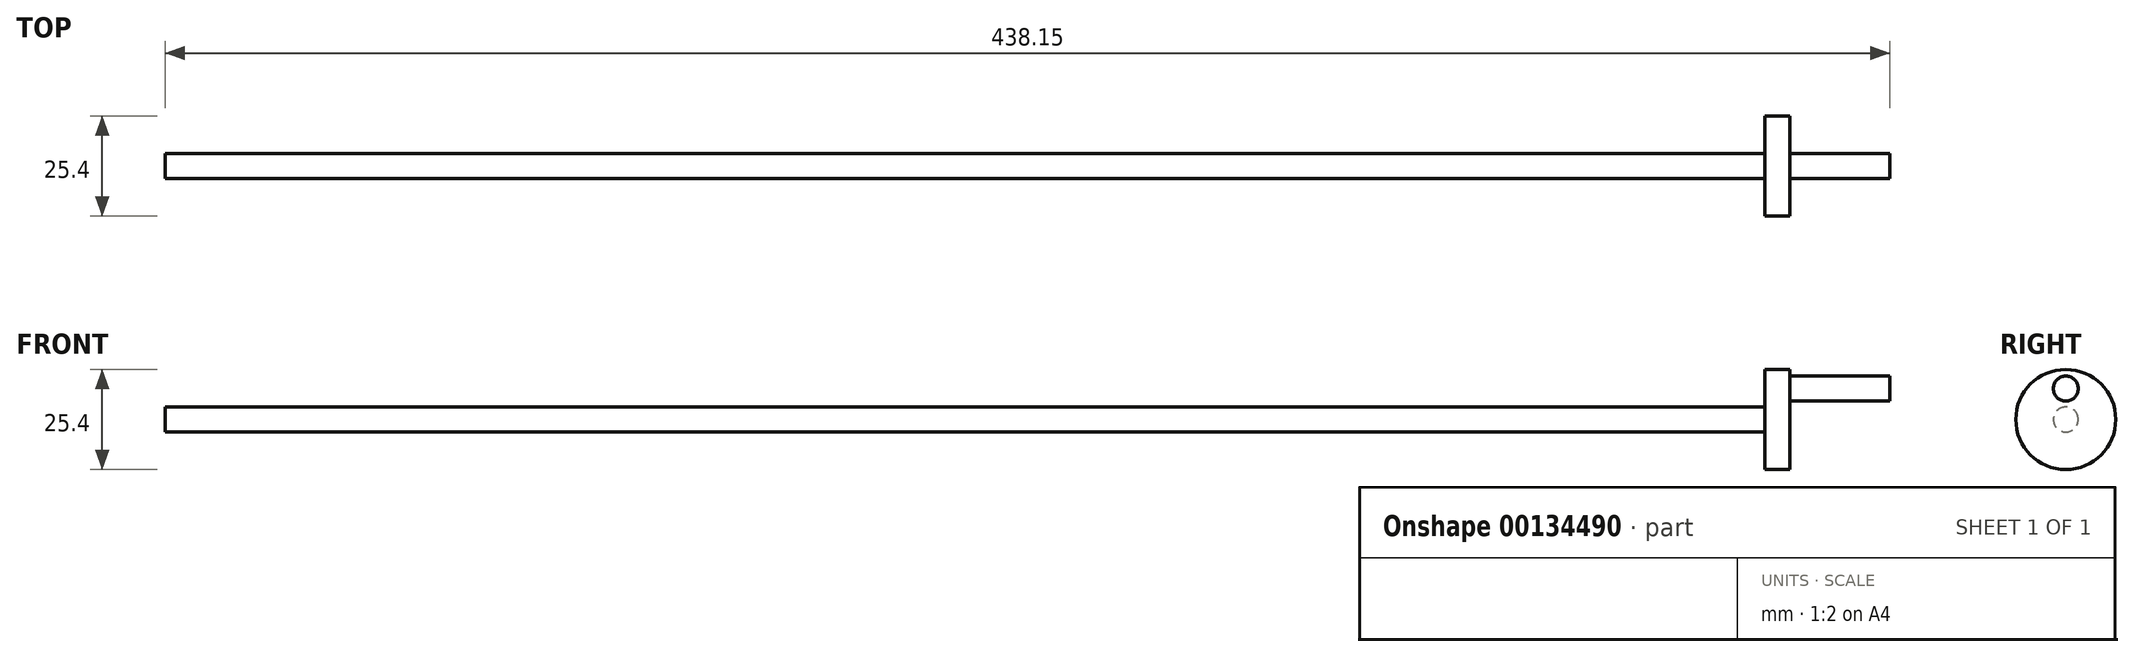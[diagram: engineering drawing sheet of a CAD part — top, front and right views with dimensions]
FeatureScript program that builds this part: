
annotation { "Feature Type Name" : "Feature", "Feature Type Description" : "" }
export const myFeature = defineFeature(function(context is Context, id is Id, definition is map)
    precondition{}
    {
        {
            var Q0;
            Q0=qCreatedBy(makeId("Right.planeOp"),FACE);
            var sketch = newSketch(context, id + "F0", { "sketchPlane" : qUnion([Q0])});
            skCircle(sketch, "E0", {"center": v(0, 0) * mm, "radius": 3.18 * mm});
            skSolve(sketch);
        }
        {
            var Q0;
            Q0 = qSketchRegion(id + "F0", true);
            extrude(context, id + "F1", {"entities" : qUnion([Q0]), "endBound" : BoundingType.SYMMETRIC, "depth" : 406.4 * mm});
        }
        {
            var Q0;
            Q0=makeQuery(id+"F1.opExtrude","CAP_FACE",FACE,{"disambiguationData":[OSD([sQuery(id+"F0.wireOp",EDGE,"E0")])],"isStart":false});
            var sketch = newSketch(context, id + "F2", { "sketchPlane" : qUnion([Q0])});
            skCircle(sketch, "E1", {"center": v(0, 0) * mm, "radius": 12.7 * mm});
            skSolve(sketch);
        }
        {
            var Q0;
            Q0 = qSketchRegion(id + "F2", true);
            extrude(context, id + "F3", {"entities" : qUnion([Q0]), "operationType" : NewBodyOperationType.ADD, "depth" : 6.35 * mm});
        }
        {
            var Q0;
            Q0=makeQuery(id+"F3.opExtrude","CAP_FACE",FACE,{"disambiguationData":[OSD([sQuery(id+"F2.wireOp",EDGE,"E1")])],"isStart":false});
            var sketch = newSketch(context, id + "F4", { "sketchPlane" : qUnion([Q0])});
            skCircle(sketch, "E2", {"center": v(0, 7.85) * mm, "radius": 3.18 * mm});
            skSolve(sketch);
        }
        {
            var Q0;
            Q0 = qSketchRegion(id + "F4", true);
            extrude(context, id + "F5", {"entities" : qUnion([Q0]), "operationType" : NewBodyOperationType.ADD, "depth" : 25.4 * mm});
        }
    });
